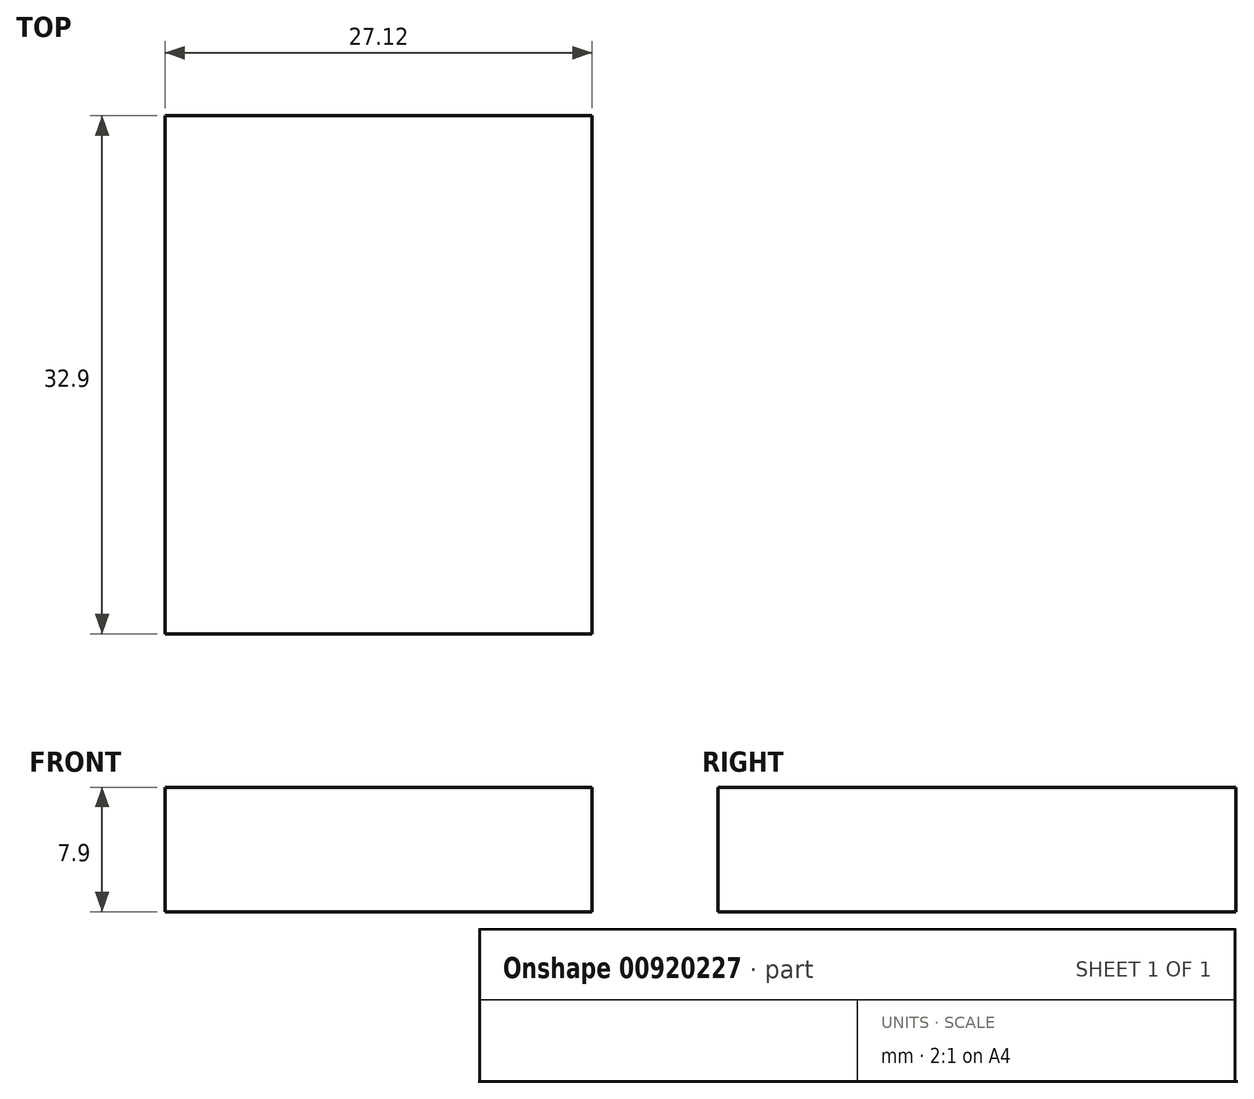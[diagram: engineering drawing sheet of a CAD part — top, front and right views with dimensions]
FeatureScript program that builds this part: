
annotation { "Feature Type Name" : "Feature", "Feature Type Description" : "" }
export const myFeature = defineFeature(function(context is Context, id is Id, definition is map)
    precondition{}
    {
        {
            var Q0;
            Q0=qCreatedBy(makeId("Top.planeOp"),FACE);
            var sketch = newSketch(context, id + "F0", { "sketchPlane" : qUnion([Q0])});
            skLineSegment(sketch, "E0.bottom", {"start": v(0, 0) * mm, "end": v(-27.12, 0) * mm});
            skLineSegment(sketch, "E0.top", {"start": v(0, -32.9) * mm, "end": v(-27.12, -32.9) * mm});
            skLineSegment(sketch, "E0.left", {"start": v(0, 0) * mm, "end": v(0, -32.9) * mm});
            skLineSegment(sketch, "E0.right", {"start": v(-27.12, 0) * mm, "end": v(-27.12, -32.9) * mm});
            skSolve(sketch);
        }
        {
            var Q0;
            Q0 = qSketchRegion(id + "F0", true);
            extrude(context, id + "F1", {"entities" : qUnion([Q0]), "depth" : 7.9 * mm, "offsetDistance" : 25 * mm});
        }
    });
